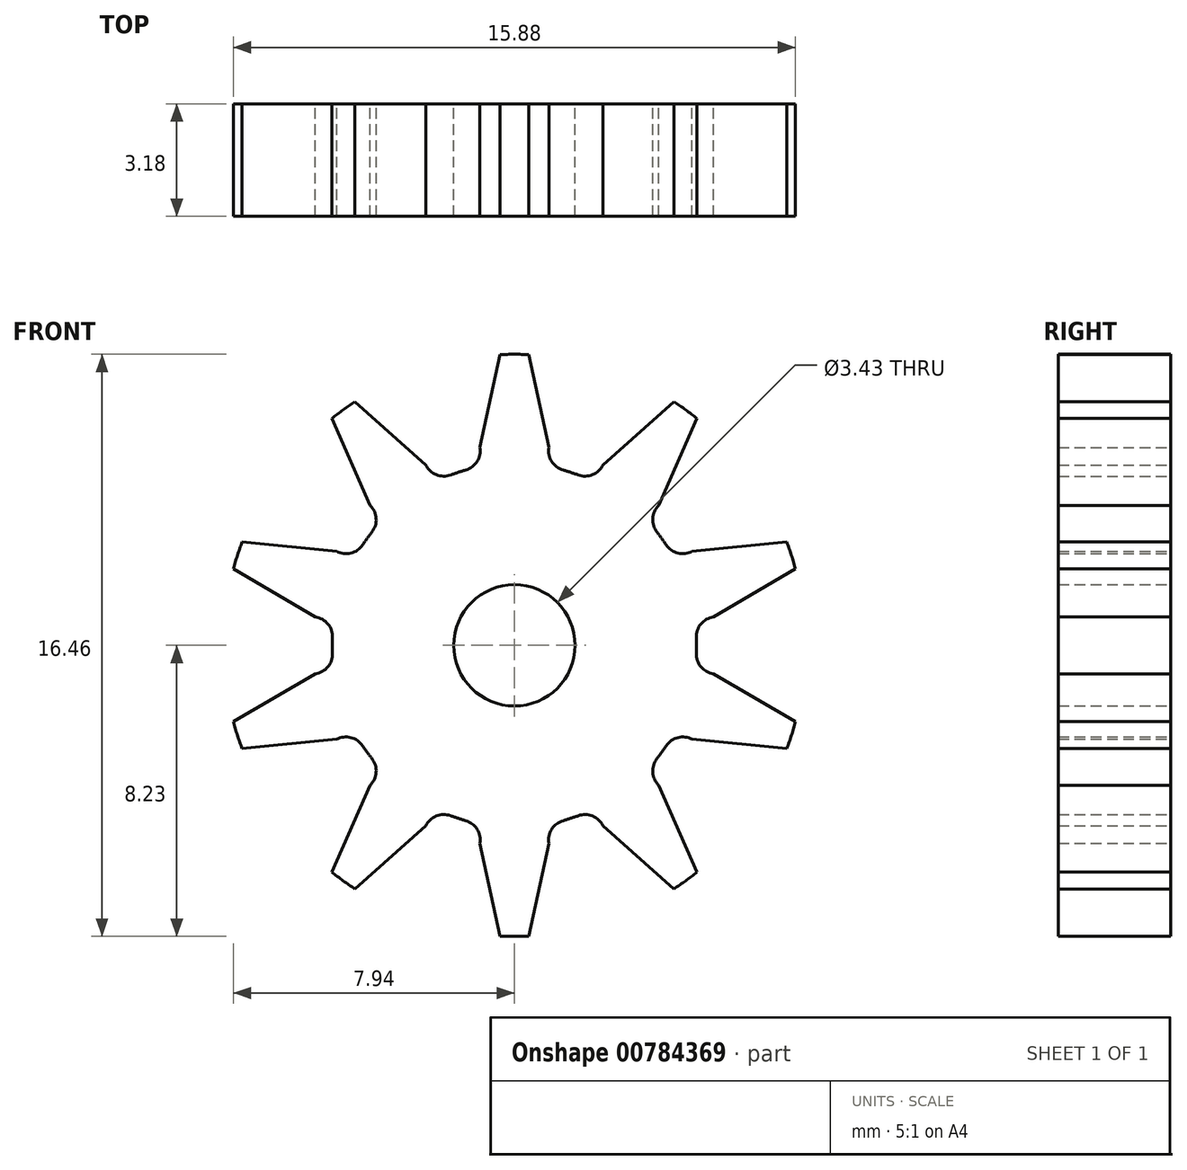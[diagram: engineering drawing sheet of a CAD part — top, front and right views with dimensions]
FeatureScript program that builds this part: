
annotation { "Feature Type Name" : "Feature", "Feature Type Description" : "" }
export const myFeature = defineFeature(function(context is Context, id is Id, definition is map)
    precondition{}
    {
        {
            var Q0;
            Q0=qCreatedBy(makeId("Front.planeOp"),FACE);
            var sketch = newSketch(context, id + "F0", { "sketchPlane" : qUnion([Q0])});
            skArc(sketch, "E0.0", {"start": v(0.4, 8.22) * mm, "mid": v(0, 8.23) * mm, "end": v(-0.4, 8.22) * mm});
            skArc(sketch, "E1.0", {"start": v(-1.38, 4.96) * mm, "mid": v(-1.05, 5.2) * mm, "end": v(-0.97, 5.6) * mm});
            skArc(sketch, "E2.0", {"start": v(0.97, 5.6) * mm, "mid": v(1.05, 5.2) * mm, "end": v(1.38, 4.96) * mm});
            skArc(sketch, "E3.0", {"start": v(1.8, 4.82) * mm, "mid": v(1.59, 4.9) * mm, "end": v(1.38, 4.96) * mm});
            skArc(sketch, "E4.0", {"start": v(1.8, 4.82) * mm, "mid": v(2.2, 4.82) * mm, "end": v(2.5, 5.1) * mm});
            skArc(sketch, "E5.0", {"start": v(5.16, 6.41) * mm, "mid": v(4.84, 6.66) * mm, "end": v(4.5, 6.89) * mm});
            skArc(sketch, "E6.0", {"start": v(5.62, 0.8) * mm, "mid": v(5.27, 0.6) * mm, "end": v(5.14, 0.22) * mm});
            skArc(sketch, "E7.0", {"start": v(5.14, -0.22) * mm, "mid": v(5.14, 0) * mm, "end": v(5.14, 0.22) * mm});
            skArc(sketch, "E8.0", {"start": v(5.14, -0.22) * mm, "mid": v(5.27, -0.6) * mm, "end": v(5.62, -0.8) * mm});
            skArc(sketch, "E9.0", {"start": v(-4.5, 6.89) * mm, "mid": v(-4.84, 6.66) * mm, "end": v(-5.16, 6.41) * mm});
            skArc(sketch, "E10.0", {"start": v(-4.03, 3.2) * mm, "mid": v(-3.9, 3.59) * mm, "end": v(-4.08, 3.96) * mm});
            skArc(sketch, "E11.0", {"start": v(-5.02, 2.66) * mm, "mid": v(-4.62, 2.6) * mm, "end": v(-4.29, 2.84) * mm});
            skArc(sketch, "E12.0", {"start": v(-4.03, 3.2) * mm, "mid": v(-4.16, 3.02) * mm, "end": v(-4.29, 2.84) * mm});
            skArc(sketch, "E13.0", {"start": v(-7.7, 2.92) * mm, "mid": v(-7.83, 2.54) * mm, "end": v(-7.94, 2.16) * mm});
            skArc(sketch, "E14.0", {"start": v(-5.14, 0.22) * mm, "mid": v(-5.27, 0.6) * mm, "end": v(-5.62, 0.8) * mm});
            skCircle(sketch, "E15.0", {"center": v(0, 0) * mm, "radius": 1.71 * mm});
            skArc(sketch, "E16.0.0", {"start": v(1.38, 4.96) * mm, "mid": v(1.05, 5.2) * mm, "end": v(0.97, 5.6) * mm});
            skArc(sketch, "E16.0.4", {"start": v(-0.97, 5.6) * mm, "mid": v(-1.05, 5.2) * mm, "end": v(-1.38, 4.96) * mm});
            skArc(sketch, "E16.0.5", {"start": v(-1.38, 4.96) * mm, "mid": v(-1.59, 4.9) * mm, "end": v(-1.8, 4.82) * mm});
            skArc(sketch, "E16.0.6", {"start": v(-1.8, 4.82) * mm, "mid": v(-2.2, 4.82) * mm, "end": v(-2.5, 5.1) * mm});
            skArc(sketch, "E16.0.10", {"start": v(-4.08, 3.96) * mm, "mid": v(-3.9, 3.59) * mm, "end": v(-4.03, 3.2) * mm});
            skArc(sketch, "E16.0.12", {"start": v(-4.29, 2.84) * mm, "mid": v(-4.62, 2.6) * mm, "end": v(-5.02, 2.66) * mm});
            skArc(sketch, "E16.0.16", {"start": v(-5.62, 0.8) * mm, "mid": v(-5.27, 0.6) * mm, "end": v(-5.14, 0.22) * mm});
            skArc(sketch, "E16.0.17", {"start": v(-5.14, 0.22) * mm, "mid": v(-5.14, 0) * mm, "end": v(-5.14, -0.22) * mm});
            skArc(sketch, "E16.0.18", {"start": v(-5.14, -0.22) * mm, "mid": v(-5.27, -0.6) * mm, "end": v(-5.62, -0.8) * mm});
            skArc(sketch, "E16.0.20", {"start": v(-7.94, -2.16) * mm, "mid": v(-7.83, -2.54) * mm, "end": v(-7.7, -2.92) * mm});
            skArc(sketch, "E16.0.22", {"start": v(-5.02, -2.66) * mm, "mid": v(-4.62, -2.6) * mm, "end": v(-4.29, -2.84) * mm});
            skArc(sketch, "E16.0.23", {"start": v(-4.29, -2.84) * mm, "mid": v(-4.16, -3.02) * mm, "end": v(-4.03, -3.2) * mm});
            skArc(sketch, "E16.0.24", {"start": v(-4.03, -3.2) * mm, "mid": v(-3.9, -3.59) * mm, "end": v(-4.08, -3.96) * mm});
            skArc(sketch, "E16.0.26", {"start": v(-5.16, -6.41) * mm, "mid": v(-4.84, -6.66) * mm, "end": v(-4.5, -6.89) * mm});
            skArc(sketch, "E16.0.28", {"start": v(-2.5, -5.1) * mm, "mid": v(-2.2, -4.82) * mm, "end": v(-1.8, -4.82) * mm});
            skArc(sketch, "E16.0.29", {"start": v(-1.8, -4.82) * mm, "mid": v(-1.59, -4.9) * mm, "end": v(-1.38, -4.96) * mm});
            skArc(sketch, "E16.0.30", {"start": v(-1.38, -4.96) * mm, "mid": v(-1.05, -5.2) * mm, "end": v(-0.97, -5.6) * mm});
            skArc(sketch, "E16.0.32", {"start": v(-0.4, -8.22) * mm, "mid": v(0, -8.23) * mm, "end": v(0.4, -8.22) * mm});
            skArc(sketch, "E16.0.34", {"start": v(0.97, -5.6) * mm, "mid": v(1.05, -5.2) * mm, "end": v(1.38, -4.96) * mm});
            skArc(sketch, "E16.0.35", {"start": v(1.38, -4.96) * mm, "mid": v(1.59, -4.9) * mm, "end": v(1.8, -4.82) * mm});
            skArc(sketch, "E16.0.36", {"start": v(1.8, -4.82) * mm, "mid": v(2.2, -4.82) * mm, "end": v(2.5, -5.1) * mm});
            skArc(sketch, "E16.0.38", {"start": v(4.5, -6.89) * mm, "mid": v(4.84, -6.66) * mm, "end": v(5.16, -6.41) * mm});
            skArc(sketch, "E16.0.40", {"start": v(4.08, -3.96) * mm, "mid": v(3.9, -3.59) * mm, "end": v(4.03, -3.2) * mm});
            skArc(sketch, "E16.0.41", {"start": v(4.03, -3.2) * mm, "mid": v(4.16, -3.02) * mm, "end": v(4.29, -2.84) * mm});
            skArc(sketch, "E16.0.42", {"start": v(4.29, -2.84) * mm, "mid": v(4.62, -2.6) * mm, "end": v(5.02, -2.66) * mm});
            skArc(sketch, "E16.0.44", {"start": v(7.7, -2.92) * mm, "mid": v(7.83, -2.54) * mm, "end": v(7.94, -2.16) * mm});
            skArc(sketch, "E16.0.46", {"start": v(5.62, -0.8) * mm, "mid": v(5.27, -0.6) * mm, "end": v(5.14, -0.22) * mm});
            skArc(sketch, "E16.0.48", {"start": v(5.14, 0.22) * mm, "mid": v(5.27, 0.6) * mm, "end": v(5.62, 0.8) * mm});
            skArc(sketch, "E16.0.50", {"start": v(7.94, 2.16) * mm, "mid": v(7.83, 2.54) * mm, "end": v(7.7, 2.92) * mm});
            skArc(sketch, "E16.0.52", {"start": v(5.02, 2.66) * mm, "mid": v(4.62, 2.6) * mm, "end": v(4.29, 2.84) * mm});
            skArc(sketch, "E16.0.53", {"start": v(4.29, 2.84) * mm, "mid": v(4.16, 3.02) * mm, "end": v(4.03, 3.2) * mm});
            skArc(sketch, "E16.0.54", {"start": v(4.03, 3.2) * mm, "mid": v(3.9, 3.59) * mm, "end": v(4.08, 3.96) * mm});
            skArc(sketch, "E16.0.58", {"start": v(2.5, 5.1) * mm, "mid": v(2.2, 4.82) * mm, "end": v(1.8, 4.82) * mm});
            skLineSegment(sketch, "E17", {"start": v(-7.7, 2.92) * mm, "end": v(-5.02, 2.66) * mm});
            skLineSegment(sketch, "E18", {"start": v(-7.94, 2.16) * mm, "end": v(-5.62, 0.8) * mm});
            skLineSegment(sketch, "E19", {"start": v(-5.62, -0.8) * mm, "end": v(-7.94, -2.16) * mm});
            skLineSegment(sketch, "E20", {"start": v(-7.7, -2.92) * mm, "end": v(-5.02, -2.66) * mm});
            skLineSegment(sketch, "E21", {"start": v(-5.16, 6.41) * mm, "end": v(-4.08, 3.96) * mm});
            skLineSegment(sketch, "E22", {"start": v(-4.08, -3.96) * mm, "end": v(-5.16, -6.41) * mm});
            skLineSegment(sketch, "E23", {"start": v(-4.5, -6.89) * mm, "end": v(-2.5, -5.1) * mm});
            skLineSegment(sketch, "E24", {"start": v(-0.97, -5.6) * mm, "end": v(-0.4, -8.22) * mm});
            skLineSegment(sketch, "E25", {"start": v(0.4, -8.22) * mm, "end": v(0.97, -5.6) * mm});
            skLineSegment(sketch, "E26", {"start": v(2.5, -5.1) * mm, "end": v(4.5, -6.89) * mm});
            skLineSegment(sketch, "E27", {"start": v(4.08, -3.96) * mm, "end": v(5.16, -6.41) * mm});
            skLineSegment(sketch, "E28", {"start": v(7.7, -2.92) * mm, "end": v(5.02, -2.66) * mm});
            skLineSegment(sketch, "E29", {"start": v(7.94, -2.16) * mm, "end": v(5.62, -0.8) * mm});
            skLineSegment(sketch, "E30", {"start": v(5.02, 2.66) * mm, "end": v(7.7, 2.92) * mm});
            skLineSegment(sketch, "E31", {"start": v(7.94, 2.16) * mm, "end": v(5.62, 0.8) * mm});
            skLineSegment(sketch, "E32", {"start": v(-4.5, 6.89) * mm, "end": v(-2.5, 5.1) * mm});
            skLineSegment(sketch, "E33", {"start": v(-0.4, 8.22) * mm, "end": v(-0.97, 5.6) * mm});
            skLineSegment(sketch, "E34", {"start": v(0.4, 8.22) * mm, "end": v(0.97, 5.6) * mm});
            skLineSegment(sketch, "E35", {"start": v(2.5, 5.1) * mm, "end": v(4.5, 6.89) * mm});
            skLineSegment(sketch, "E36", {"start": v(5.16, 6.41) * mm, "end": v(4.08, 3.96) * mm});
            skSolve(sketch);
        }
        {
            var Q0;
            Q0=makeQuery(id+"F0.imprint","IMPRINT",FACE,{"disambiguationData":[TD([[makeQuery(id+"F0.imprint","IMPRINT",EDGE,{"derivedFrom":sQuery(id+"F0.wireOp",EDGE,"E15.0")}),-1.0]])]});
            extrude(context, id + "F1", {"entities" : qUnion([Q0]), "depth" : 3.17 * mm, "offsetDistance" : 25.4 * mm});
        }
    });
